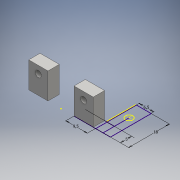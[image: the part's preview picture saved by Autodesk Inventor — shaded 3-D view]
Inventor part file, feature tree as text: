
AUTODESK INVENTOR PART (.ipt)
format: ipt  version: 2016 (Build 200138000, 138)  size: 179,200 bytes
history: native  units: mm
features: sketch x7, extrude x4, plane x1, hole x1
ambient origin geometry x8: Origin, YZ Plane, XZ Plane, XY Plane, X Axis, Y Axis, Z Axis, Center Point
bodies: Solid1 (feature_tree)
feature tree (13):
  sketch  "Sketch1"  dims[d7=2.5mm d13=7.5mm]
  sketch  "Sketch2"  dims[d14=11.5mm d16=2.0mm]
  plane  "Work Plane2"
  sketch  "Sketch3"  dims[d17=3.0mm d23=5.0mm]
  sketch  "Sketch4"  dims[d24=6.5mm d25=29.8mm]
  extrude  "Extrusion1"  Depth=2.5mm
  extrude  "Extrusion2"  Depth=11.5mm
  hole  "Hole1"  [1 undecoded]
  extrude  "Extrusion8"  Depth=29.8mm
  extrude  "Extrusion9"  Depth=18.5mm
  sketch  "Sketch10"  dims[d30=-6.75mm d31=10.1mm d32=6.5mm d33=2.5mm d34=0.0mm d35=2.5mm d36=0.0mm d37=2.7mm d38=6.0mm d39=4.0mm d40=2.0mm d41=90.0deg d42=8.0mm d43=20.594885mm d69=1.75mm d70=0.9mm d71=1.75mm d72=0.9mm d73=2.5mm d74=0.0mm d75=5.0mm d76=0.0mm d78=9.5mm d79=5.0mm d80=6.5mm d81=18.0mm]
  sketch  "Sketch5"  dims[d26=13.0mm d27=18.5mm]
  sketch  "Sketch8"  dims[d28=3.2mm]
note: 1 required parameter value undecoded (feature->parameter linkage not recoverable at this tier; creation-order binding heuristic only, values carry confidence <= 0.55)
